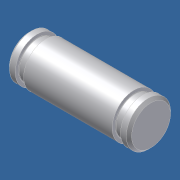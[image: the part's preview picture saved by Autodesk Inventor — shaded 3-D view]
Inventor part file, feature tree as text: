
AUTODESK INVENTOR PART (.ipt)
format: ipt  version: unknown  size: 210,944 bytes
history: native  units: in
note: dims shown in document units (in); Inventor stores cm internally (conversion verified against a paired STEP export)
features: other x49, revolve x1, sketch x1
ambient origin geometry x8: Origin, YZ Plane, XZ Plane, XY Plane, X Axis, Y Axis, Z Axis, Center Point
feature tree (51):
  revolve  "Revolution1"  [1 undecoded]
  other  "pin_XY"
  other  "pin_YZ"
  other  "pin_ZX"
  other  "pin_X"
  other  "pin_Y"
  other  "pin_Z"
  other  "pin_Center"
  other  "rr1_XY"
  other  "rr1_YZ"
  other  "rr1_ZX"
  other  "rr1_X"
  other  "rr1_Y"
  other  "rr1_Z"
  other  "rr1_Center"
  other  "rr2_XY"
  other  "rr2_YZ"
  other  "rr2_ZX"
  other  "rr2_X"
  other  "rr2_Y"
  other  "rr2_Z"
  other  "rr2_Center"
  other  "w21_XY"
  other  "w21_YZ"
  other  "w21_ZX"
  other  "w21_X"
  other  "w21_Y"
  other  "w21_Z"
  other  "w21_Center"
  other  "w22_XY"
  other  "w22_YZ"
  other  "w22_ZX"
  other  "w22_X"
  other  "w22_Y"
  other  "w22_Z"
  other  "w22_Center"
  other  "p1_XY"
  other  "p1_YZ"
  other  "p1_ZX"
  other  "p1_X"
  other  "p1_Y"
  other  "p1_Z"
  other  "p1_Center"
  other  "p2_XY"
  other  "p2_YZ"
  other  "p2_ZX"
  other  "p2_X"
  other  "p2_Y"
  other  "p2_Z"
  other  "p2_Center"
  sketch  "Sketch_1"  dims[d0=360.0deg]
note: 1 required parameter value undecoded (feature->parameter linkage not recoverable at this tier; creation-order binding heuristic only, values carry confidence <= 0.55)
